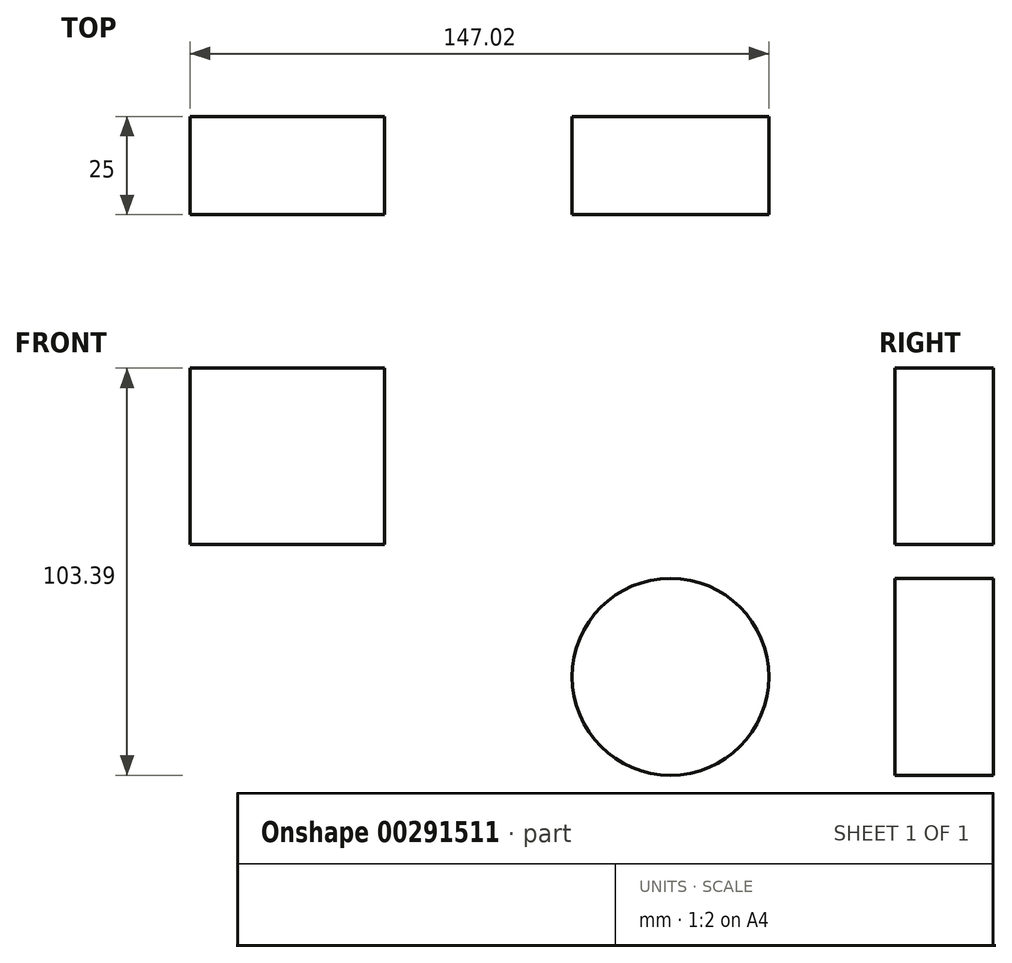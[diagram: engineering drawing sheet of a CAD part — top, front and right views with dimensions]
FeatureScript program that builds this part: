
annotation { "Feature Type Name" : "Feature", "Feature Type Description" : "" }
export const myFeature = defineFeature(function(context is Context, id is Id, definition is map)
    precondition{}
    {
        {
            var Q0;
            Q0=qCreatedBy(makeId("Front.planeOp"),FACE);
            var sketch = newSketch(context, id + "F0", { "sketchPlane" : qUnion([Q0])});
            skLineSegment(sketch, "E0.bottom", {"start": v(-93.15, 5.57) * mm, "end": v(-43.82, 5.57) * mm});
            skLineSegment(sketch, "E0.top", {"start": v(-93.15, 50.32) * mm, "end": v(-43.82, 50.32) * mm});
            skLineSegment(sketch, "E0.left", {"start": v(-93.15, 5.57) * mm, "end": v(-93.15, 50.32) * mm});
            skLineSegment(sketch, "E0.right", {"start": v(-43.82, 5.57) * mm, "end": v(-43.82, 50.32) * mm});
            skPoint(sketch, "E0.middle", {"position": v(-68.48, 27.94) * mm});
            skSolve(sketch);
        }
        {
            var Q0;
            Q0=makeQuery(id+"F0.imprint","IMPRINT",FACE,{"disambiguationData":[TD([[makeQuery(id+"F0.imprint","IMPRINT",EDGE,{"derivedFrom":sQuery(id+"F0.wireOp",EDGE,"E0.bottom")}),1.0]])]});
            extrude(context, id + "F1", {"entities" : qUnion([Q0]), "depth" : 25 * mm});
        }
        {
            var Q0;
            Q0=qCreatedBy(makeId("Front.planeOp"),FACE);
            var sketch = newSketch(context, id + "F2", { "sketchPlane" : qUnion([Q0])});
            skLineSegment(sketch, "E1.bottom", {"start": v(52.58, 3.17) * mm, "end": v(98.67, 3.17) * mm});
            skLineSegment(sketch, "E1.top", {"start": v(52.58, 45.68) * mm, "end": v(98.67, 45.68) * mm});
            skLineSegment(sketch, "E1.left", {"start": v(52.58, 3.17) * mm, "end": v(52.58, 45.68) * mm});
            skLineSegment(sketch, "E1.right", {"start": v(98.67, 3.17) * mm, "end": v(98.67, 45.68) * mm});
            skPoint(sketch, "E1.middle", {"position": v(75.62, 24.43) * mm});
            skSolve(sketch);
        }
        {
            var Q0;
            Q0=qCreatedBy(makeId("Front.planeOp"),FACE);
            var sketch = newSketch(context, id + "F3", { "sketchPlane" : qUnion([Q0])});
            skCircle(sketch, "E2", {"center": v(28.87, -28.07) * mm, "radius": 25 * mm});
            skSolve(sketch);
        }
        {
            var Q0;
            Q0=makeQuery(id+"F3.imprint","IMPRINT",FACE,{"disambiguationData":[TD([[makeQuery(id+"F3.imprint","IMPRINT",EDGE,{"derivedFrom":sQuery(id+"F3.wireOp",EDGE,"E2")}),1.0]])]});
            extrude(context, id + "F4", {"entities" : qUnion([Q0]), "depth" : 25 * mm});
        }
    });
